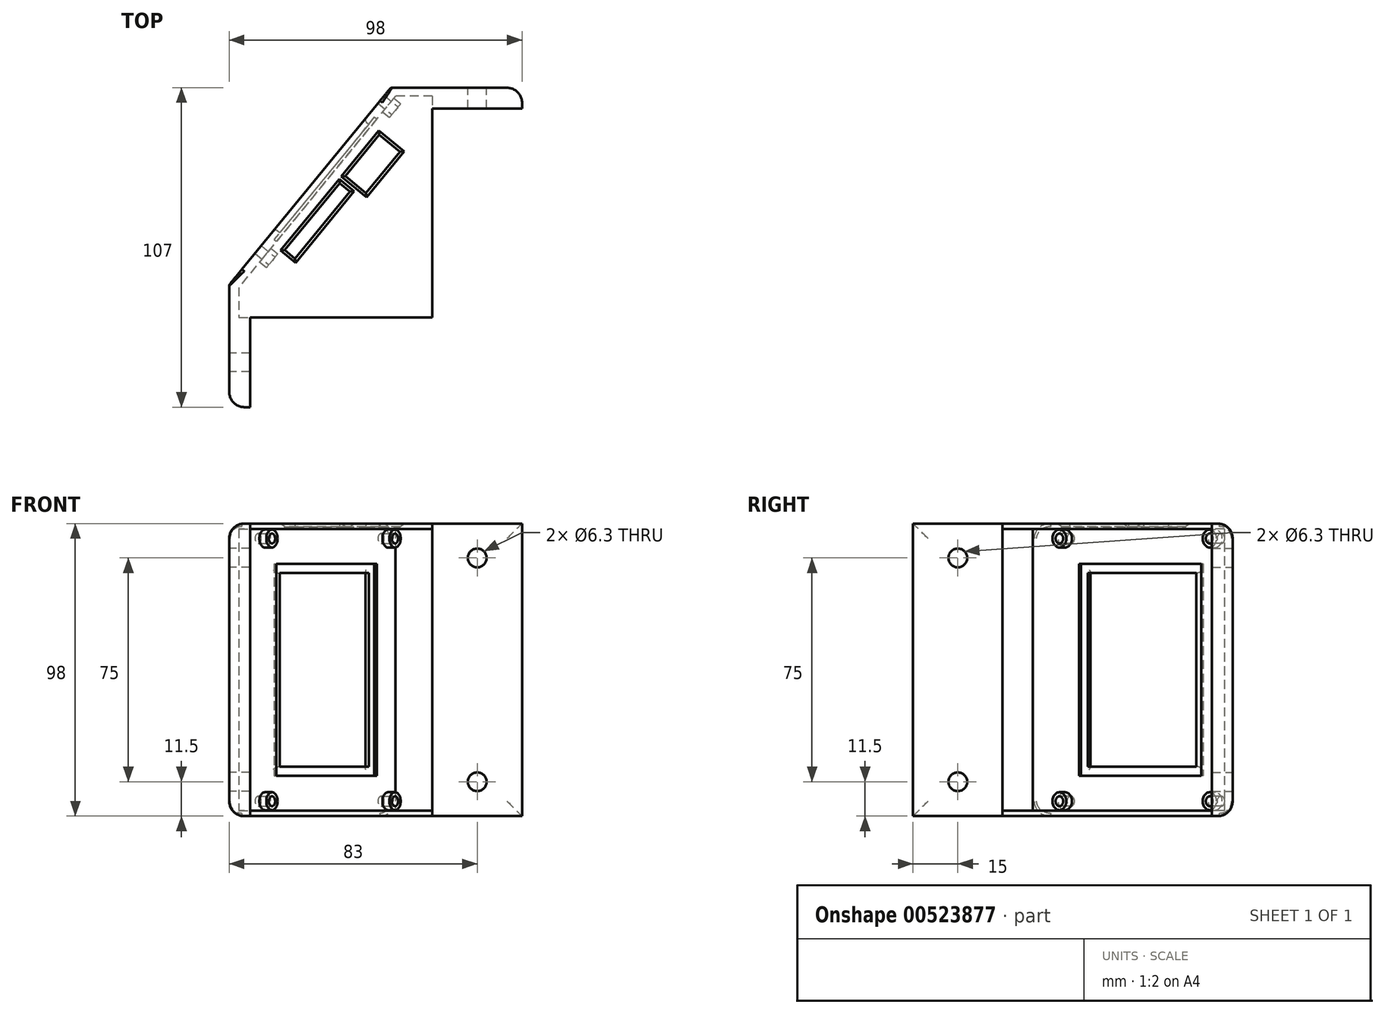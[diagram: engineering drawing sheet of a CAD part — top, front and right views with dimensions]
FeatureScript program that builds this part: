
annotation { "Feature Type Name" : "Feature", "Feature Type Description" : "" }
export const myFeature = defineFeature(function(context is Context, id is Id, definition is map)
    precondition{}
    {
        {
            var Q0;
            Q0=qCreatedBy(makeId("Top.planeOp"),FACE);
            var sketch = newSketch(context, id + "F0", { "sketchPlane" : qUnion([Q0])});
            skLineSegment(sketch, "E0.bottom", {"start": v(0, 0) * mm, "end": v(30, 0) * mm, "construction": true});
            skLineSegment(sketch, "E0.top", {"start": v(0, 30) * mm, "end": v(30, 30) * mm, "construction": true});
            skLineSegment(sketch, "E0.left", {"start": v(0, 0) * mm, "end": v(0, 30) * mm, "construction": true});
            skLineSegment(sketch, "E0.right", {"start": v(30, 0) * mm, "end": v(30, 30) * mm, "construction": true});
            skLineSegment(sketch, "E1.bottom", {"start": v(61, 70) * mm, "end": v(91, 70) * mm, "construction": true});
            skLineSegment(sketch, "E1.top", {"start": v(61, 100) * mm, "end": v(91, 100) * mm, "construction": true});
            skLineSegment(sketch, "E1.left", {"start": v(61, 70) * mm, "end": v(61, 100) * mm, "construction": true});
            skLineSegment(sketch, "E1.right", {"start": v(91, 70) * mm, "end": v(91, 100) * mm, "construction": true});
            skLineSegment(sketch, "E2", {"start": v(61, 70) * mm, "end": v(61, 100) * mm});
            skLineSegment(sketch, "E3", {"start": v(60.77, 119.05) * mm, "end": v(-24.85, 14.49) * mm});
            skLineSegment(sketch, "E4", {"start": v(61, 94.07) * mm, "end": v(8.54, 30) * mm, "construction": true});
            skLineSegment(sketch, "E5", {"start": v(61, 94.07) * mm, "end": v(48.62, 104.2) * mm, "construction": true});
            skLineSegment(sketch, "E6", {"start": v(8.54, 30) * mm, "end": v(-3.84, 40.14) * mm, "construction": true});
            skLineSegment(sketch, "E7", {"start": v(-4.85, 0) * mm, "end": v(0, 0) * mm});
            skLineSegment(sketch, "E8", {"start": v(51.37, 112.3) * mm, "end": v(-39.42, 1.43) * mm});
            skLineSegment(sketch, "E9", {"start": v(91, 100) * mm, "end": v(91, 107) * mm});
            skLineSegment(sketch, "E10", {"start": v(91, 107) * mm, "end": v(47.03, 107) * mm});
            skLineSegment(sketch, "E11", {"start": v(0, 0) * mm, "end": v(-7, 0) * mm});
            skLineSegment(sketch, "E12", {"start": v(-7, 0) * mm, "end": v(-7, 41.02) * mm});
            skLineSegment(sketch, "E13", {"start": v(91, 100) * mm, "end": v(61, 100) * mm});
            skLineSegment(sketch, "E14", {"start": v(61, 104.2) * mm, "end": v(61, 100) * mm});
            skLineSegment(sketch, "E15", {"start": v(61, 104.2) * mm, "end": v(48.62, 104.2) * mm});
            skLineSegment(sketch, "E16", {"start": v(-3.84, 40.14) * mm, "end": v(-3.84, 30) * mm});
            skLineSegment(sketch, "E17", {"start": v(-3.84, 30) * mm, "end": v(0, 30) * mm});
            skLineSegment(sketch, "E18", {"start": v(0, 30) * mm, "end": v(0, 0) * mm});
            skSolve(sketch);
        }
        {
            var Q0;
            Q0=qSketchRegion(id+"F0",true);
            extrude(context, id + "F1", {"entities" : qUnion([Q0]), "depth" : 98 * mm, "offsetDistance" : 25 * mm});
        }
        {
            var Q0;
            Q0=makeQuery(id+"F1.opExtrude","SWEPT_FACE",FACE,{"disambiguationData":[OSD([sQuery(id+"F0.wireOp",EDGE,"E3")])]});
            var sketch = newSketch(context, id + "F2", { "sketchPlane" : qUnion([Q0])});
            skLineSegment(sketch, "E19", {"start": v(70.02, 98) * mm, "end": v(70.02, 0) * mm, "construction": true});
            skLineSegment(sketch, "E20", {"start": v(111.43, 49) * mm, "end": v(28.62, 49) * mm, "construction": true});
            skLineSegment(sketch, "E21.bottom", {"start": v(98.52, 81.5) * mm, "end": v(51.52, 81.5) * mm});
            skLineSegment(sketch, "E21.top", {"start": v(98.52, 16.5) * mm, "end": v(51.52, 16.5) * mm});
            skLineSegment(sketch, "E21.left", {"start": v(98.52, 81.5) * mm, "end": v(98.52, 16.5) * mm});
            skLineSegment(sketch, "E21.right", {"start": v(51.52, 81.5) * mm, "end": v(51.52, 16.5) * mm});
            skLineSegment(sketch, "E22.0", {"start": v(48.52, 84.5) * mm, "end": v(48.52, 13.5) * mm});
            skLineSegment(sketch, "E22.1", {"start": v(101.52, 84.5) * mm, "end": v(48.52, 84.5) * mm});
            skLineSegment(sketch, "E22.2", {"start": v(101.52, 84.5) * mm, "end": v(101.52, 13.5) * mm});
            skLineSegment(sketch, "E22.3", {"start": v(101.52, 13.5) * mm, "end": v(48.52, 13.5) * mm});
            skSolve(sketch);
        }
        {
            var Q0;
            Q0=makeQuery(id+"F2.imprint","IMPRINT",FACE,{"disambiguationData":[TD([[makeQuery(id+"F2.imprint","IMPRINT",EDGE,{"derivedFrom":sQuery(id+"F2.wireOp",EDGE,"E21.bottom")}),1.0]])]});
            extrude(context, id + "F3", {"entities" : qUnion([Q0]), "operationType" : NewBodyOperationType.REMOVE, "oppositeDirection" : true, "depth" : 25 * mm, "offsetDistance" : 25 * mm});
        }
        {
            var Q0;
            Q0=makeQuery(id+"F2.imprint","IMPRINT",FACE,{"disambiguationData":[TD([[makeQuery(id+"F2.imprint","IMPRINT",EDGE,{"derivedFrom":sQuery(id+"F2.wireOp",EDGE,"E21.bottom")}),-1.0]])]});
            extrude(context, id + "F4", {"entities" : qUnion([Q0]), "operationType" : NewBodyOperationType.REMOVE, "oppositeDirection" : true, "depth" : 1 * mm, "offsetDistance" : 25 * mm});
        }
        {
            var Q0;
            Q0=makeQuery(id+"F2.imprint","IMPRINT",FACE,{"disambiguationData":[TD([[makeQuery(id+"F2.imprint","IMPRINT",EDGE,{"derivedFrom":sQuery(id+"F2.wireOp",EDGE,"E21.bottom")}),-1.0]])]});
            var sketch = newSketch(context, id + "F5", { "sketchPlane" : qUnion([Q0])});
            skLineSegment(sketch, "E23", {"start": v(75.02, 88.6) * mm, "end": v(75.02, 4.4) * mm, "construction": true});
            skCircle(sketch, "E24", {"center": v(107.52, 5) * mm, "radius": 1.65 * mm});
            skCircle(sketch, "E25", {"center": v(42.52, 5) * mm, "radius": 1.65 * mm});
            skCircle(sketch, "E26.MirrorC", {"center": v(107.52, 93) * mm, "radius": 1.65 * mm});
            skCircle(sketch, "E27.MirrorC", {"center": v(42.52, 93) * mm, "radius": 1.65 * mm});
            skSolve(sketch);
        }
        {
            var Q0;
            Q0=qSketchRegion(id+"F5",true);
            extrude(context, id + "F6", {"entities" : qUnion([Q0]), "operationType" : NewBodyOperationType.REMOVE, "oppositeDirection" : true, "depth" : 25 * mm, "offsetDistance" : 25 * mm});
        }
        {
            var Q0;
            Q0=makeQuery(id+"F2.imprint","IMPRINT",FACE,{"disambiguationData":[TD([[makeQuery(id+"F2.imprint","IMPRINT",EDGE,{"derivedFrom":sQuery(id+"F2.wireOp",EDGE,"E22.0")}),-1.0]])]});
            var sketch = newSketch(context, id + "F7", { "sketchPlane" : qUnion([Q0])});
            skCircle(sketch, "E28", {"center": v(107.52, 93) * mm, "radius": 3 * mm});
            skCircle(sketch, "E29", {"center": v(42.52, 93) * mm, "radius": 3 * mm});
            skCircle(sketch, "E30", {"center": v(107.52, 93) * mm, "radius": 1.65 * mm});
            skCircle(sketch, "E31", {"center": v(42.52, 93) * mm, "radius": 1.65 * mm});
            skCircle(sketch, "E32.MirrorC", {"center": v(107.52, 5) * mm, "radius": 1.65 * mm});
            skCircle(sketch, "E33.MirrorC", {"center": v(42.52, 5) * mm, "radius": 1.65 * mm});
            skCircle(sketch, "E34.MirrorC", {"center": v(107.52, 5) * mm, "radius": 3 * mm});
            skCircle(sketch, "E35.MirrorC", {"center": v(42.52, 5) * mm, "radius": 3 * mm});
            skSolve(sketch);
        }
        {
            var Q0;
            Q0=qSketchRegion(id+"F7",true);
            extrude(context, id + "F8", {"entities" : qUnion([Q0]), "operationType" : NewBodyOperationType.ADD, "depth" : 3 * mm, "offsetDistance" : 25 * mm});
        }
        {
            var Q0;
            Q0=makeQuery(id+"F3.boolean.opBoolean","INTERSECT",EDGE,{"derivedFrom":[makeQuery(id+"F1.opExtrude","SWEPT_FACE",FACE,{"disambiguationData":[OSD([sQuery(id+"F0.wireOp",EDGE,"E8")])]}),makeQuery(id+"F3.opExtrude","SWEPT_FACE",FACE,{"disambiguationData":[OSD([sQuery(id+"F2.wireOp",EDGE,"E21.left")])]})]});
            var Q1;
            Q1=makeQuery(id+"F3.boolean.opBoolean","INTERSECT",EDGE,{"derivedFrom":[makeQuery(id+"F1.opExtrude","SWEPT_FACE",FACE,{"disambiguationData":[OSD([sQuery(id+"F0.wireOp",EDGE,"E8")])]}),makeQuery(id+"F3.opExtrude","SWEPT_FACE",FACE,{"disambiguationData":[OSD([sQuery(id+"F2.wireOp",EDGE,"E21.bottom")])]})]});
            var Q2;
            Q2=makeQuery(id+"F3.boolean.opBoolean","INTERSECT",EDGE,{"derivedFrom":[makeQuery(id+"F1.opExtrude","SWEPT_FACE",FACE,{"disambiguationData":[OSD([sQuery(id+"F0.wireOp",EDGE,"E8")])]}),makeQuery(id+"F3.opExtrude","SWEPT_FACE",FACE,{"disambiguationData":[OSD([sQuery(id+"F2.wireOp",EDGE,"E21.right")])]})]});
            var Q3;
            Q3=makeQuery(id+"F3.boolean.opBoolean","INTERSECT",EDGE,{"derivedFrom":[makeQuery(id+"F1.opExtrude","SWEPT_FACE",FACE,{"disambiguationData":[OSD([sQuery(id+"F0.wireOp",EDGE,"E8")])]}),makeQuery(id+"F3.opExtrude","SWEPT_FACE",FACE,{"disambiguationData":[OSD([sQuery(id+"F2.wireOp",EDGE,"E21.top")])]})]});
            fillet(context, id + "F9", {"entities" : qUnion([Q0, Q1, Q2, Q3]), "radius" : 1 * mm, "tangentPropagation" : true, "allowEdgeOverflow" : false});
        }
        {
            var Q0;
            Q0=makeQuery(id+"F1.opExtrude","SWEPT_FACE",FACE,{"disambiguationData":[OSD([sQuery(id+"F0.wireOp",EDGE,"E10")])]});
            var sketch = newSketch(context, id + "F10", { "sketchPlane" : qUnion([Q0])});
            skCircle(sketch, "E36", {"center": v(-76, 86.5) * mm, "radius": 3.15 * mm});
            skCircle(sketch, "E37", {"center": v(-76, 11.5) * mm, "radius": 3.15 * mm});
            skSolve(sketch);
        }
        {
            var Q0;
            Q0=qSketchRegion(id+"F10",true);
            extrude(context, id + "F11", {"entities" : qUnion([Q0]), "operationType" : NewBodyOperationType.REMOVE, "oppositeDirection" : true, "depth" : 25 * mm, "offsetDistance" : 25 * mm});
        }
        {
            var Q0;
            Q0=makeQuery(id+"F1.opExtrude","SWEPT_FACE",FACE,{"disambiguationData":[OSD([sQuery(id+"F0.wireOp",EDGE,"E12")])]});
            var sketch = newSketch(context, id + "F12", { "sketchPlane" : qUnion([Q0])});
            skCircle(sketch, "E38", {"center": v(-15, 86.5) * mm, "radius": 3.15 * mm});
            skCircle(sketch, "E39", {"center": v(-15, 11.5) * mm, "radius": 3.15 * mm});
            skSolve(sketch);
        }
        {
            var Q0;
            Q0=qSketchRegion(id+"F12",true);
            extrude(context, id + "F13", {"entities" : qUnion([Q0]), "operationType" : NewBodyOperationType.REMOVE, "oppositeDirection" : true, "depth" : 25 * mm, "offsetDistance" : 25 * mm});
        }
        {
            var Q0;
            Q0=makeQuery(id+"F1.opExtrude","CAP_FACE",FACE,{"disambiguationData":[OSD([sQuery(id+"F0.wireOp",EDGE,"E3"),sQuery(id+"F0.wireOp",EDGE,"E8"),sQuery(id+"F0.wireOp",EDGE,"E9"),sQuery(id+"F0.wireOp",EDGE,"E10"),sQuery(id+"F0.wireOp",EDGE,"E11"),sQuery(id+"F0.wireOp",EDGE,"E12"),sQuery(id+"F0.wireOp",EDGE,"E13"),sQuery(id+"F0.wireOp",EDGE,"E14"),sQuery(id+"F0.wireOp",EDGE,"E15"),sQuery(id+"F0.wireOp",EDGE,"E16"),sQuery(id+"F0.wireOp",EDGE,"E17"),sQuery(id+"F0.wireOp",EDGE,"E18")])],"isStart":true});
            var sketch = newSketch(context, id + "F14", { "sketchPlane" : qUnion([Q0])});
            skLineSegment(sketch, "E40.bottom", {"start": v(0, 0) * mm, "end": v(30, 0) * mm, "construction": true});
            skLineSegment(sketch, "E40.top", {"start": v(0, -30) * mm, "end": v(30, -30) * mm, "construction": true});
            skLineSegment(sketch, "E40.left", {"start": v(0, 0) * mm, "end": v(0, -30) * mm, "construction": true});
            skLineSegment(sketch, "E40.right", {"start": v(30, 0) * mm, "end": v(30, -30) * mm, "construction": true});
            skLineSegment(sketch, "E41.bottom", {"start": v(61, -100) * mm, "end": v(91, -100) * mm, "construction": true});
            skLineSegment(sketch, "E41.top", {"start": v(61, -70) * mm, "end": v(91, -70) * mm, "construction": true});
            skLineSegment(sketch, "E41.left", {"start": v(61, -100) * mm, "end": v(61, -70) * mm, "construction": true});
            skLineSegment(sketch, "E41.right", {"start": v(91, -100) * mm, "end": v(91, -70) * mm, "construction": true});
            skLineSegment(sketch, "E42", {"start": v(-3.84, -30) * mm, "end": v(61, -30) * mm});
            skLineSegment(sketch, "E43", {"start": v(61, -30) * mm, "end": v(61, -104.2) * mm});
            skLineSegment(sketch, "E44", {"start": v(61, -104.2) * mm, "end": v(48.62, -104.2) * mm});
            skLineSegment(sketch, "E45", {"start": v(48.62, -104.2) * mm, "end": v(-3.84, -40.14) * mm});
            skLineSegment(sketch, "E46", {"start": v(-3.84, -40.14) * mm, "end": v(-3.84, -30) * mm});
            skSolve(sketch);
        }
        {
            var Q0;
            Q0=qSketchRegion(id+"F14",true);
            extrude(context, id + "F15", {"entities" : qUnion([Q0]), "operationType" : NewBodyOperationType.ADD, "oppositeDirection" : true, "depth" : 1.8 * mm, "offsetDistance" : 25 * mm});
        }
        {
            var Q0;
            Q0=makeQuery(id+"F1.opExtrude","CAP_FACE",FACE,{"disambiguationData":[OSD([sQuery(id+"F0.wireOp",EDGE,"E3"),sQuery(id+"F0.wireOp",EDGE,"E8"),sQuery(id+"F0.wireOp",EDGE,"E9"),sQuery(id+"F0.wireOp",EDGE,"E10"),sQuery(id+"F0.wireOp",EDGE,"E11"),sQuery(id+"F0.wireOp",EDGE,"E12"),sQuery(id+"F0.wireOp",EDGE,"E13"),sQuery(id+"F0.wireOp",EDGE,"E14"),sQuery(id+"F0.wireOp",EDGE,"E15"),sQuery(id+"F0.wireOp",EDGE,"E16"),sQuery(id+"F0.wireOp",EDGE,"E17"),sQuery(id+"F0.wireOp",EDGE,"E18")])],"isStart":false});
            var sketch = newSketch(context, id + "F16", { "sketchPlane" : qUnion([Q0])});
            skLineSegment(sketch, "E47", {"start": v(61, 104.2) * mm, "end": v(61, 30) * mm});
            skLineSegment(sketch, "E48", {"start": v(61, 30) * mm, "end": v(-3.84, 30) * mm});
            skLineSegment(sketch, "E49", {"start": v(-3.84, 30) * mm, "end": v(-3.84, 40.14) * mm});
            skLineSegment(sketch, "E50", {"start": v(-3.84, 40.14) * mm, "end": v(48.62, 104.2) * mm});
            skLineSegment(sketch, "E51", {"start": v(48.62, 104.2) * mm, "end": v(61, 104.2) * mm});
            skLineSegment(sketch, "E52", {"start": v(43.22, 91.3) * mm, "end": v(46.32, 88.77) * mm});
            skLineSegment(sketch, "E53", {"start": v(31.82, 77.38) * mm, "end": v(34.55, 75.14) * mm});
            skLineSegment(sketch, "E54", {"start": v(29.92, 75.05) * mm, "end": v(33.4, 72.2) * mm});
            skLineSegment(sketch, "E55", {"start": v(11.55, 52.62) * mm, "end": v(14.98, 49.8) * mm});
            skLineSegment(sketch, "E56", {"start": v(43.22, 91.3) * mm, "end": v(31.82, 77.38) * mm});
            skLineSegment(sketch, "E57", {"start": v(50.19, 85.6) * mm, "end": v(38.78, 71.67) * mm});
            skLineSegment(sketch, "E58", {"start": v(46.32, 88.77) * mm, "end": v(50.19, 85.6) * mm});
            skLineSegment(sketch, "E59", {"start": v(34.55, 75.14) * mm, "end": v(38.78, 71.67) * mm});
            skLineSegment(sketch, "E60", {"start": v(33.4, 72.2) * mm, "end": v(15.03, 49.77) * mm});
            skLineSegment(sketch, "E61.trimOffspring", {"start": v(29.92, 75.05) * mm, "end": v(11.55, 52.62) * mm});
            skPoint(sketch, "E62.orphan", {"position": v(40.13, 93.84) * mm});
            skPoint(sketch, "E63.orphan", {"position": v(8.45, 55.15) * mm});
            skLineSegment(sketch, "E64", {"start": v(15.03, 49.77) * mm, "end": v(14.98, 49.8) * mm});
            skSolve(sketch);
        }
        {
            var Q0;
            Q0=qSketchRegion(id+"F16",true);
            extrude(context, id + "F17", {"entities" : qUnion([Q0]), "operationType" : NewBodyOperationType.ADD, "oppositeDirection" : true, "depth" : 1.8 * mm, "offsetDistance" : 25 * mm});
        }
        {
            var Q0;
            Q0=makeQuery(id+"F1.opExtrude","SWEPT_EDGE",EDGE,{"disambiguationData":[OSD([sQuery(id+"F0.wireOp",EDGE,"E9"),sQuery(id+"F0.wireOp",EDGE,"E10")])]});
            var Q1;
            Q1=makeQuery(id+"F1.opExtrude","CAP_EDGE",EDGE,{"disambiguationData":[OSD([sQuery(id+"F0.wireOp",EDGE,"E10")])],"isStart":true});
            var Q2;
            Q2=makeQuery(id+"F1.opExtrude","CAP_EDGE",EDGE,{"disambiguationData":[OSD([sQuery(id+"F0.wireOp",EDGE,"E10")])],"isStart":false});
            var Q3;
            Q3=makeQuery(id+"F1.opExtrude","CAP_EDGE",EDGE,{"disambiguationData":[OSD([sQuery(id+"F0.wireOp",EDGE,"E12")])],"isStart":false});
            var Q4;
            Q4=makeQuery(id+"F1.opExtrude","SWEPT_EDGE",EDGE,{"disambiguationData":[OSD([sQuery(id+"F0.wireOp",EDGE,"E11"),sQuery(id+"F0.wireOp",EDGE,"E12")])]});
            var Q5;
            Q5=makeQuery(id+"F1.opExtrude","CAP_EDGE",EDGE,{"disambiguationData":[OSD([sQuery(id+"F0.wireOp",EDGE,"E12")])],"isStart":true});
            fillet(context, id + "F18", {"entities" : qUnion([Q0, Q1, Q2, Q3, Q4, Q5]), "radius" : 5 * mm, "tangentPropagation" : true, "allowEdgeOverflow" : false});
        }
        {
            var Q0;
            Q0=makeQuery(id+"F1.opExtrude","CAP_EDGE",EDGE,{"disambiguationData":[OSD([sQuery(id+"F0.wireOp",EDGE,"E8")])],"isStart":false});
            fillet(context, id + "F19", {"entities" : qUnion([Q0]), "radius" : 1 * mm, "tangentPropagation" : true, "allowEdgeOverflow" : false});
        }
        {
            var Q0;
            Q0=makeQuery(id+"F17.opExtrude","CAP_EDGE",EDGE,{"disambiguationData":[OSD([sQuery(id+"F16.wireOp",EDGE,"E57")])],"isStart":true});
            var Q1;
            Q1=makeQuery(id+"F17.opExtrude","CAP_EDGE",EDGE,{"disambiguationData":[OSD([sQuery(id+"F16.wireOp",EDGE,"E52"),sQuery(id+"F16.wireOp",EDGE,"E58")])],"isStart":true});
            var Q2;
            Q2=makeQuery(id+"F17.opExtrude","CAP_EDGE",EDGE,{"disambiguationData":[OSD([sQuery(id+"F16.wireOp",EDGE,"E56")])],"isStart":true});
            var Q3;
            Q3=makeQuery(id+"F17.opExtrude","CAP_EDGE",EDGE,{"disambiguationData":[OSD([sQuery(id+"F16.wireOp",EDGE,"E53"),sQuery(id+"F16.wireOp",EDGE,"E59")])],"isStart":true});
            var Q4;
            Q4=makeQuery(id+"F17.opExtrude","CAP_EDGE",EDGE,{"disambiguationData":[OSD([sQuery(id+"F16.wireOp",EDGE,"E54")])],"isStart":true});
            var Q5;
            Q5=makeQuery(id+"F17.opExtrude","CAP_EDGE",EDGE,{"disambiguationData":[OSD([sQuery(id+"F16.wireOp",EDGE,"E60")])],"isStart":true});
            var Q6;
            Q6=makeQuery(id+"F17.opExtrude","CAP_EDGE",EDGE,{"disambiguationData":[OSD([sQuery(id+"F16.wireOp",EDGE,"E61.trimOffspring")])],"isStart":true});
            var Q7;
            Q7=makeQuery(id+"F17.opExtrude","CAP_EDGE",EDGE,{"disambiguationData":[OSD([sQuery(id+"F16.wireOp",EDGE,"E55"),sQuery(id+"F16.wireOp",EDGE,"E64")])],"isStart":true});
            chamfer(context, id + "F20", {"entities" : qUnion([Q0, Q1, Q2, Q3, Q4, Q5, Q6, Q7]), "width" : 1 * mm, "tangentPropagation" : true});
        }
    });
